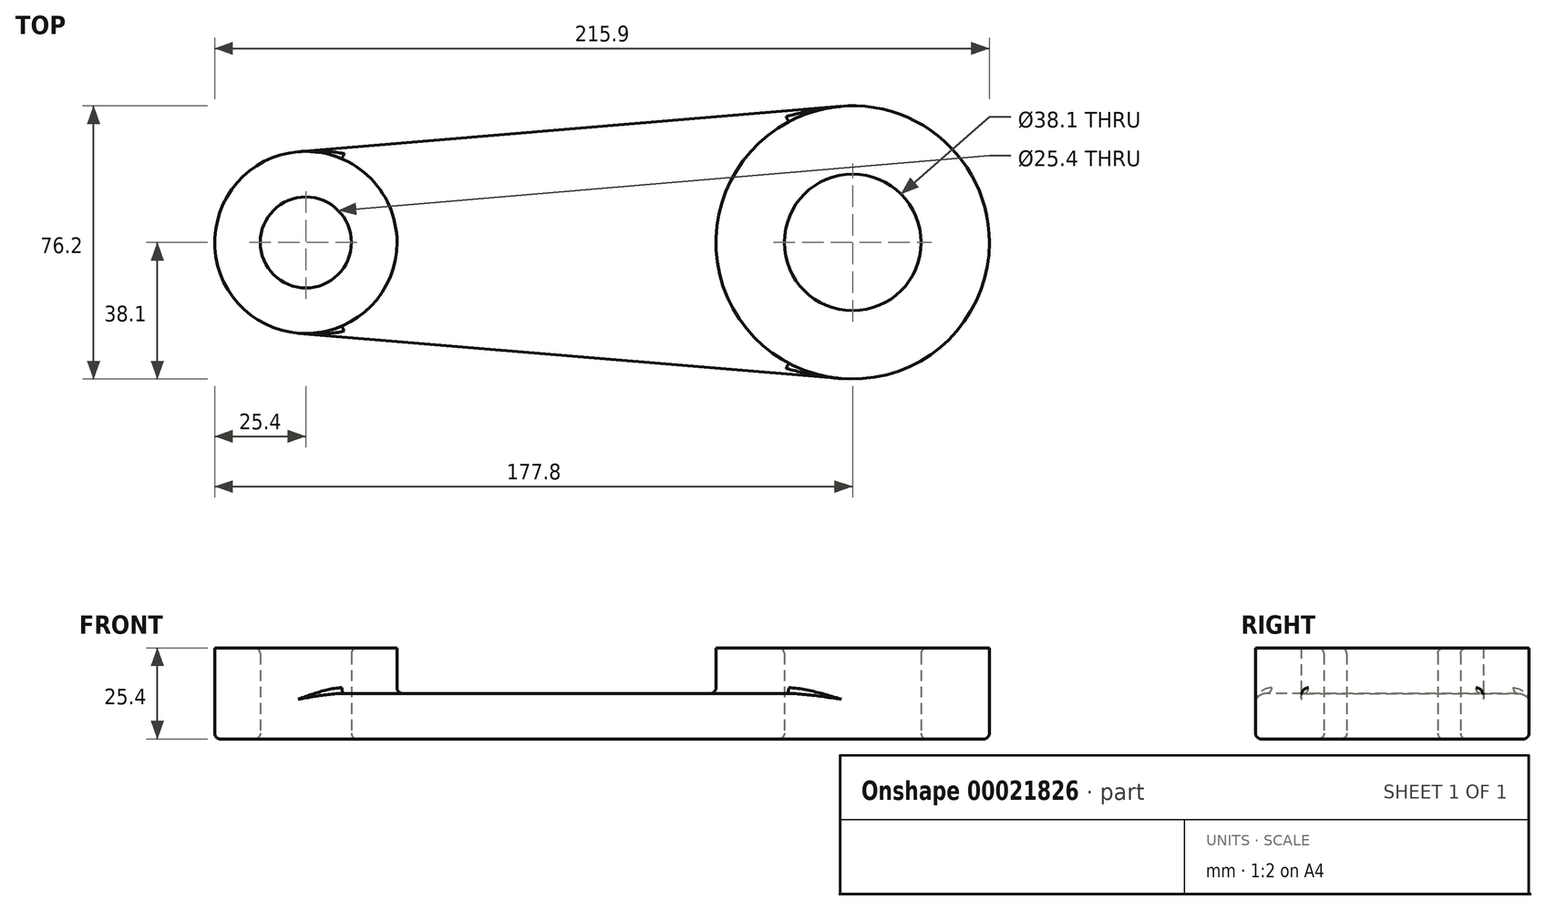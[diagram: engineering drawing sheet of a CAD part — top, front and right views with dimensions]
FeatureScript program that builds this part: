
annotation { "Feature Type Name" : "Feature", "Feature Type Description" : "" }
export const myFeature = defineFeature(function(context is Context, id is Id, definition is map)
    precondition{}
    {
        {
            var Q0;
            Q0=qCreatedBy(makeId("Top.planeOp"),FACE);
            var sketch = newSketch(context, id + "F0", { "sketchPlane" : qUnion([Q0])});
            skCircle(sketch, "E0", {"center": v(0, 0) * mm, "radius": 38.1 * mm});
            skCircle(sketch, "E1", {"center": v(-152.4, 0) * mm, "radius": 25.4 * mm});
            skLineSegment(sketch, "E2", {"start": v(-154.52, 25.31) * mm, "end": v(-3.18, 37.97) * mm});
            skLineSegment(sketch, "E3", {"start": v(-154.52, -25.31) * mm, "end": v(-3.18, -37.97) * mm});
            skCircle(sketch, "E4", {"center": v(-152.4, 0) * mm, "radius": 12.7 * mm});
            skCircle(sketch, "E5", {"center": v(0, 0) * mm, "radius": 19.05 * mm});
            skSolve(sketch);
        }
        {
            var Q0;
            {var subQ0=sQuery(id+"F0.wireOp",EDGE,"E1");var subQ2=makeQuery(id+"F0.imprint","INTERSECT",VERTEX,{"derivedFrom":[subQ0,sQuery(id+"F0.wireOp",EDGE,"E2")]});Q0=makeQuery(id+"F0.imprint","IMPRINT",FACE,{"disambiguationData":[TD([[makeQuery(id+"F0.imprint","IMPRINT",EDGE,{"disambiguationData":[TD([[subQ2,-1.0]])],"derivedFrom":subQ0}),1.0]])]});}
            var Q1;
            {var subQ0=sQuery(id+"F0.wireOp",EDGE,"E0");var subQ2=makeQuery(id+"F0.imprint","INTERSECT",VERTEX,{"derivedFrom":[subQ0,sQuery(id+"F0.wireOp",EDGE,"E2")]});Q1=makeQuery(id+"F0.imprint","IMPRINT",FACE,{"disambiguationData":[TD([[makeQuery(id+"F0.imprint","IMPRINT",EDGE,{"disambiguationData":[TD([[subQ2,-1.0]])],"derivedFrom":subQ0}),1.0]])]});}
            var Q2;
            Q2=sQuery(id+"F0.wireOp",EDGE,"E1");
            extrude(context, id + "F1", {"entities" : qUnion([Q0, Q1]), "surfaceEntities" : qUnion([Q2]), "depth" : 25.4 * mm});
        }
        {
            var Q0;
            {var subQ1=sQuery(id+"F0.wireOp",EDGE,"E2");Q0=makeQuery(id+"F0.imprint","IMPRINT",FACE,{"disambiguationData":[TD([[makeQuery(id+"F0.imprint","IMPRINT",EDGE,{"derivedFrom":subQ1}),-1.0]])]});}
            extrude(context, id + "F2", {"entities" : qUnion([Q0]), "operationType" : NewBodyOperationType.ADD, "depth" : 12.7 * mm});
        }
        {
            var Q0;
            Q0=makeQuery(id+"F2.opExtrude","CAP_FACE",FACE,{"disambiguationData":[OSD([sQuery(id+"F0.wireOp",EDGE,"E0"),sQuery(id+"F0.wireOp",EDGE,"E1"),sQuery(id+"F0.wireOp",EDGE,"E2"),sQuery(id+"F0.wireOp",EDGE,"E3")])],"isStart":false});
            var Q1;
            {var subQ0=sQuery(id+"F0.wireOp",EDGE,"E0");var subQ1=sQuery(id+"F0.wireOp",EDGE,"E1");Q1=makeQuery(id+"F2.boolean.opBoolean","MERGE",FACE,{"derivedFrom":[makeQuery(id+"F1.opExtrude","CAP_FACE",FACE,{"disambiguationData":[OSD([subQ0])],"isStart":true}),makeQuery(id+"F1.opExtrude","CAP_FACE",FACE,{"disambiguationData":[OSD([subQ1])],"isStart":true}),makeQuery(id+"F2.opExtrude","CAP_FACE",FACE,{"disambiguationData":[OSD([subQ0,subQ1,sQuery(id+"F0.wireOp",EDGE,"E2"),sQuery(id+"F0.wireOp",EDGE,"E3")])],"isStart":true})]});}
            var Q2;
            Q2=makeQuery(id+"F1.opExtrude","SWEPT_FACE",FACE,{"disambiguationData":[OSD([sQuery(id+"F0.wireOp",EDGE,"E5")])]});
            var Q3;
            Q3=makeQuery(id+"F1.opExtrude","SWEPT_FACE",FACE,{"disambiguationData":[OSD([sQuery(id+"F0.wireOp",EDGE,"E4")])]});
            fillet(context, id + "F3", {"entities" : qUnion([Q0, Q1, Q2, Q3]), "radius" : 1.59 * mm, "tangentPropagation" : true, "allowEdgeOverflow" : false});
        }
    });
